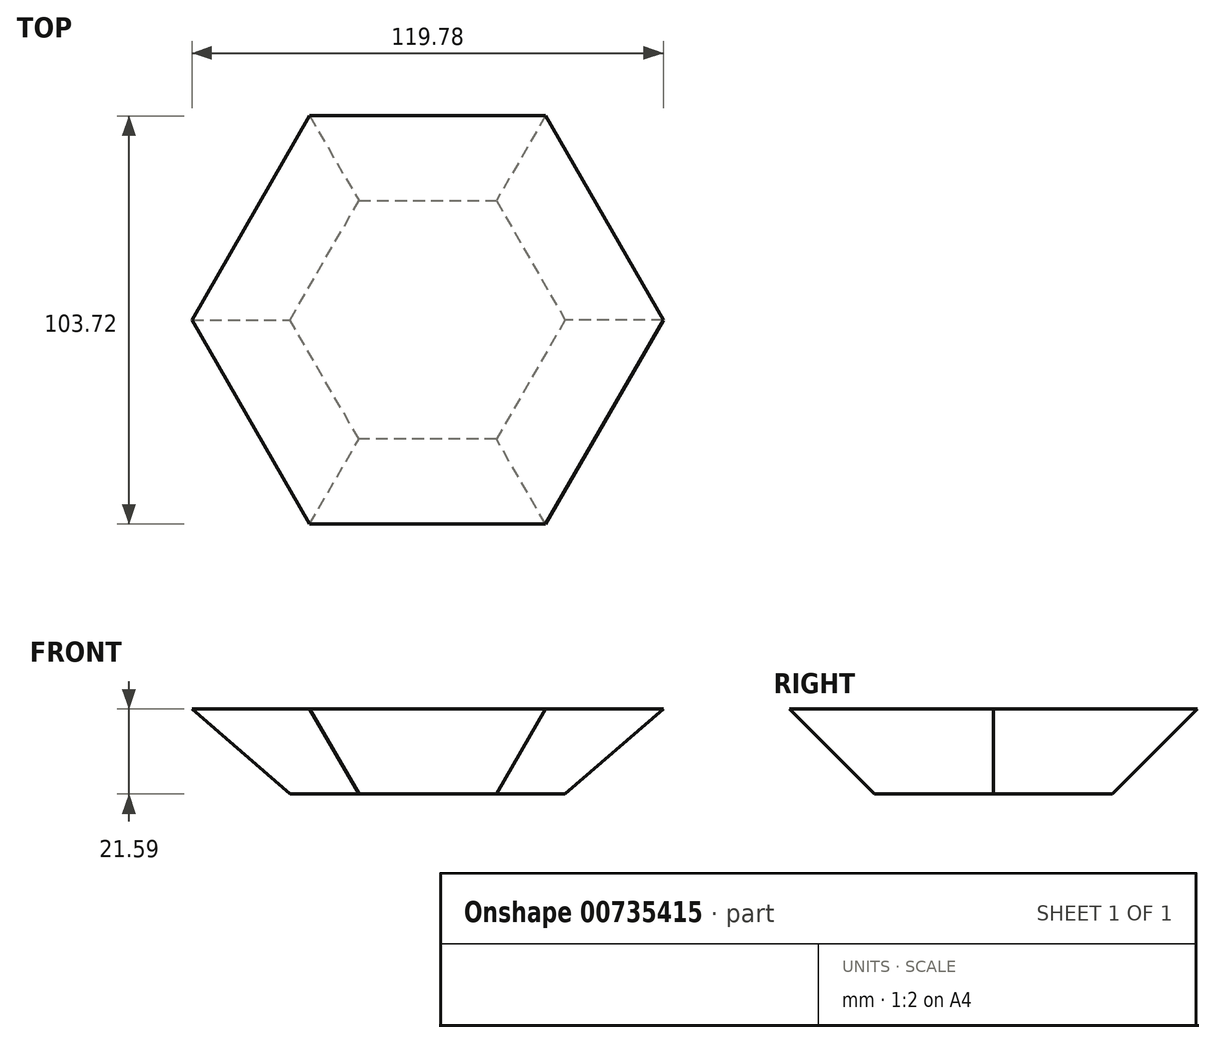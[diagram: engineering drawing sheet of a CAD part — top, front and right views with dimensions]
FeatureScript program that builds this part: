
annotation { "Feature Type Name" : "Feature", "Feature Type Description" : "" }
export const myFeature = defineFeature(function(context is Context, id is Id, definition is map)
    precondition{}
    {
        {
            var Q0;
            Q0=qCreatedBy(makeId("Top.planeOp"),FACE);
            var sketch = newSketch(context, id + "F0", { "sketchPlane" : qUnion([Q0])});
            skLineSegment(sketch, "E0", {"start": v(34.96, 0) * mm, "end": v(0, 0) * mm});
            skLineSegment(sketch, "E1.MirrorCS", {"start": v(-34.96, 0) * mm, "end": v(0, 0) * mm});
            skCircle(sketch, "E2.cCircle", {"center": v(0, 0) * mm, "radius": 34.96 * mm, "construction": true});
            skLineSegment(sketch, "E2.0", {"start": v(-34.96, 0) * mm, "end": v(-17.48, 30.27) * mm});
            skLineSegment(sketch, "E2.1", {"start": v(-17.48, 30.27) * mm, "end": v(17.48, 30.27) * mm});
            skLineSegment(sketch, "E2.2", {"start": v(17.48, 30.27) * mm, "end": v(34.96, 0) * mm});
            skLineSegment(sketch, "E2.3", {"start": v(34.96, 0) * mm, "end": v(17.48, -30.27) * mm});
            skLineSegment(sketch, "E2.4", {"start": v(17.48, -30.27) * mm, "end": v(-17.48, -30.27) * mm});
            skLineSegment(sketch, "E2.5", {"start": v(-17.48, -30.27) * mm, "end": v(-34.96, 0) * mm});
            skSolve(sketch);
        }
        {
            var Q0;
            Q0=makeQuery(id+"F0.imprint","IMPRINT",FACE,{"disambiguationData":[TD([[makeQuery(id+"F0.imprint","IMPRINT",EDGE,{"derivedFrom":sQuery(id+"F0.wireOp",EDGE,"E0")}),-1.0]])]});
            var Q1;
            Q1=makeQuery(id+"F0.imprint","IMPRINT",FACE,{"disambiguationData":[TD([[makeQuery(id+"F0.imprint","IMPRINT",EDGE,{"derivedFrom":sQuery(id+"F0.wireOp",EDGE,"E0")}),1.0]])]});
            extrude(context, id + "F1", {"entities" : qUnion([Q0, Q1]), "depth" : 21.59 * mm, "offsetDistance" : 25.4 * mm, "hasDraft" : true, "draftAngle" : 45 * degree});
        }
    });
